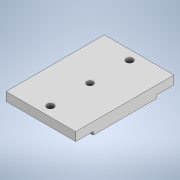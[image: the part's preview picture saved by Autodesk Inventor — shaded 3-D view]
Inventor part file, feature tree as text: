
AUTODESK INVENTOR PART (.ipt)
format: ipt  version: 2020 (Build 240168000, 168)  size: 145,408 bytes
history: native  units: mm
features: sketch x5, extrude x3, hole x2
ambient origin geometry x8: Origin, YZ Plane, XZ Plane, XY Plane, X Axis, Y Axis, Z Axis, Center Point
bodies: Solid1 (feature_tree)
feature tree (10):
  extrude  "Extrusion1"  TaperAngle=0.0deg  [1 undecoded]
  extrude  "Extrusion2"  Depth=5.4mm
  extrude  "Extrusion3"  Depth=2.4mm
  hole  "Hole1"  [1 undecoded]
  hole  "Hole2"  [1 undecoded]
  sketch  "Sketch1"  dims[d1=44.0mm d3=0.0mm]
  sketch  "Sketch2"  dims[d6=5.4mm d7=0.0mm d8=3.242mm d9=4.0mm d10=4.0mm]
  sketch  "Sketch3"  dims[d12=90.0deg d13=5.4mm d14=0.0mm]
  sketch  "Sketch4"  dims[d15=4.31mm d16=8.331mm d17=7.94mm d18=2.4mm d19=90.0deg d20=12.3mm d21=0.0mm d22=6.0mm]
  sketch  "Sketch5"  dims[d23=6.0mm d25=2.0mm d26=0.0mm d31=40.0mm d32=20.0mm d33=0.0mm d34=2.0mm d35=20.0mm]
note: 3 required parameter values undecoded (feature->parameter linkage not recoverable at this tier; creation-order binding heuristic only, values carry confidence <= 0.55)
